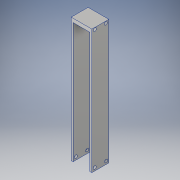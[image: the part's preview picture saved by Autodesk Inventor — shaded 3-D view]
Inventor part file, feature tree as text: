
AUTODESK INVENTOR PART (.ipt)
format: ipt  version: 2019 (Build 230136000, 136)  size: 125,952 bytes
history: native  units: in
note: dims shown in document units (in); Inventor stores cm internally (conversion verified against a paired STEP export)
features: sketch x3, hole x2, extrude x1
ambient origin geometry x8: Origin, YZ Plane, XZ Plane, XY Plane, X Axis, Y Axis, Z Axis, Center Point
bodies: Solid1 (feature_tree)
feature tree (6):
  extrude  "Extrusion1"  Depth=8.0in
  hole  "Hole1"  [1 undecoded]
  hole  "Hole3"  [1 undecoded]
  sketch  "Sketch1"  dims[d0=1.125in d1=8.0in]
  sketch  "Sketch2"  dims[d2=0.125in d3=1.125in d4=0.0in]
  sketch  "Sketch4"  dims[d5=0.205in d6=0.75in d7=1.125in d8=0.1875in d9=0.201in d10=0.38in d11=0.385in d12=0.25in d13=0.5635in d14=0.45in d15=0.8108in d24=0.25in d25=0.125in d26=0.2in d27=0.2in d28=0.725in d29=0.2in d30=0.75in d31=0.375in d32=0.25in d33=0.5635in d34=0.432in d35=0.8108in]
note: 2 required parameter values undecoded (feature->parameter linkage not recoverable at this tier; creation-order binding heuristic only, values carry confidence <= 0.55)
